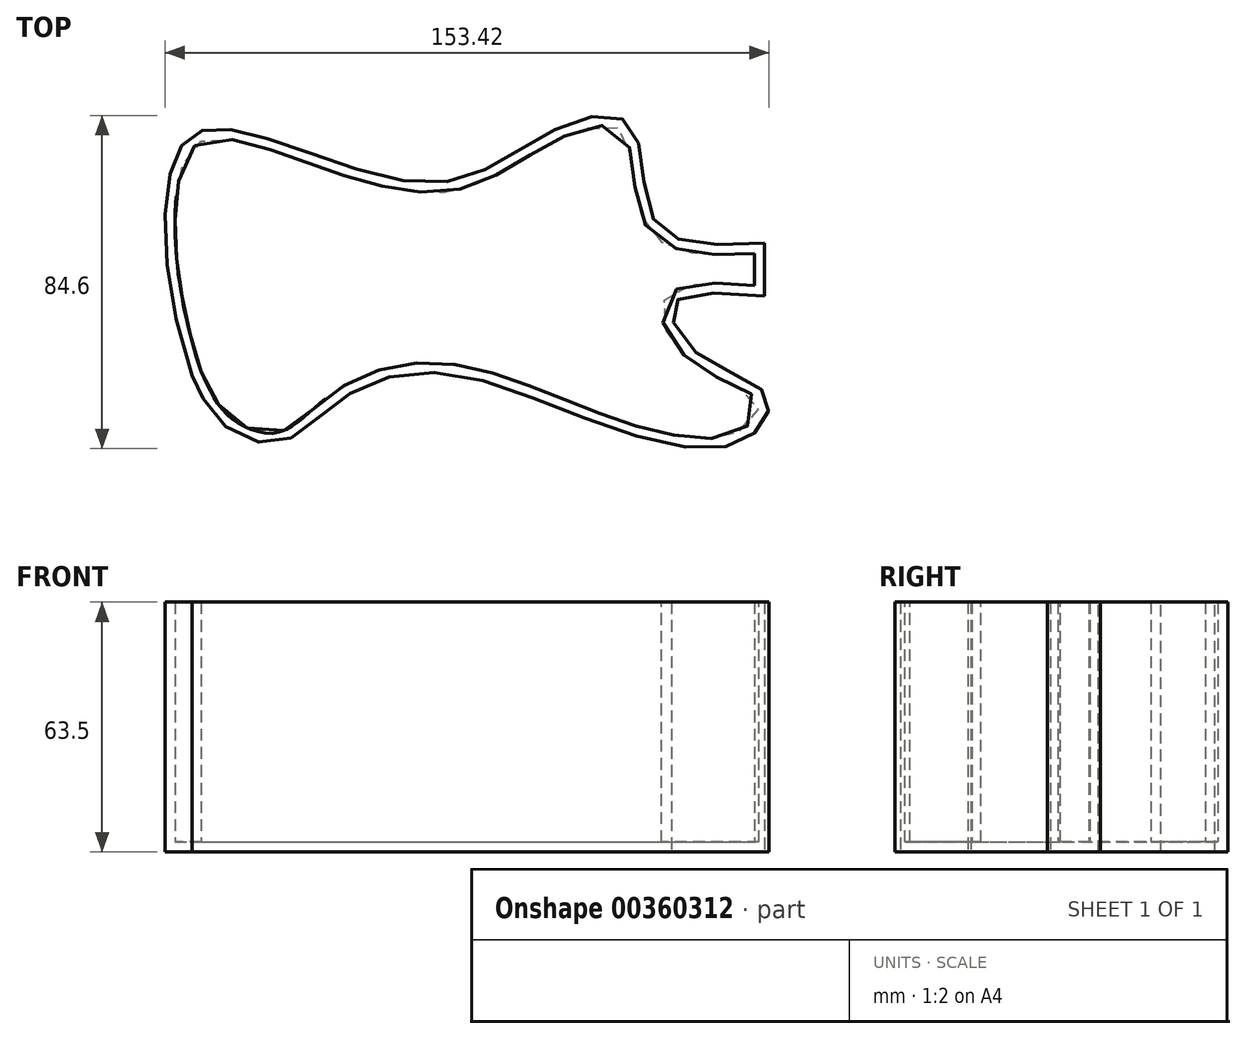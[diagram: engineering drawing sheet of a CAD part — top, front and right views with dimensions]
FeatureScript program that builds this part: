
annotation { "Feature Type Name" : "Feature", "Feature Type Description" : "" }
export const myFeature = defineFeature(function(context is Context, id is Id, definition is map)
    precondition{}
    {
        {
            var Q0;
            Q0=qCreatedBy(makeId("Top.planeOp"),FACE);
            var sketch = newSketch(context, id + "F0", { "sketchPlane" : qUnion([Q0])});
            skFitSpline(sketch, "E0", {"points": [v(-60.2, -20.15) * mm, v(-66.16, 29.53) * mm, v(-58.2, 41.9) * mm, v(-35.71, 38.23) * mm, v(4.58, 29.07) * mm, v(32.05, 42.35) * mm, v(51.28, 43.27) * mm, v(57.46, 18.77) * mm, v(85.16, 13.5) * mm], "startDerivative": vector(-112.36, 326.26) * mm, "endDerivative": vector(281.93, 18.35) * mm});
            skFitSpline(sketch, "E1", {"points": [v(-60.2, -20.15) * mm, v(-53.8, -31.13) * mm, v(-37.77, -37.09) * mm, v(-22.9, -26.56) * mm, v(2.52, -19.46) * mm, v(40.98, -31.6) * mm, v(74.17, -38.46) * mm, v(85.16, -31.82) * mm, v(85.16, -24.5) * mm, v(68.45, -14.88) * mm, v(62.04, -2.06) * mm, v(85.16, 0) * mm], "startDerivative": vector(41.58, -75.5) * mm, "endDerivative": vector(310.38, -27.6) * mm});
            skLineSegment(sketch, "E2", {"start": v(85.16, 13.5) * mm, "end": v(85.16, 0) * mm});
            skSolve(sketch);
        }
        {
            var Q0;
            Q0=makeQuery(id+"F0.imprint","IMPRINT",FACE,{"disambiguationData":[TD([[makeQuery(id+"F0.imprint","IMPRINT",EDGE,{"derivedFrom":sQuery(id+"F0.wireOp",EDGE,"E0")}),-1.0]])]});
            extrude(context, id + "F1", {"entities" : qUnion([Q0]), "depth" : 63.5 * mm});
        }
        {
            var Q0;
            Q0=makeQuery(id+"F1.opExtrude","CAP_FACE",FACE,{"disambiguationData":[OSD([sQuery(id+"F0.wireOp",EDGE,"E0"),sQuery(id+"F0.wireOp",EDGE,"E1"),sQuery(id+"F0.wireOp",EDGE,"E2")])],"isStart":false});
            shell(context, id + "F2", {"entities" : qUnion([Q0]), "thickness" : 2.5 * mm});
        }
    });
